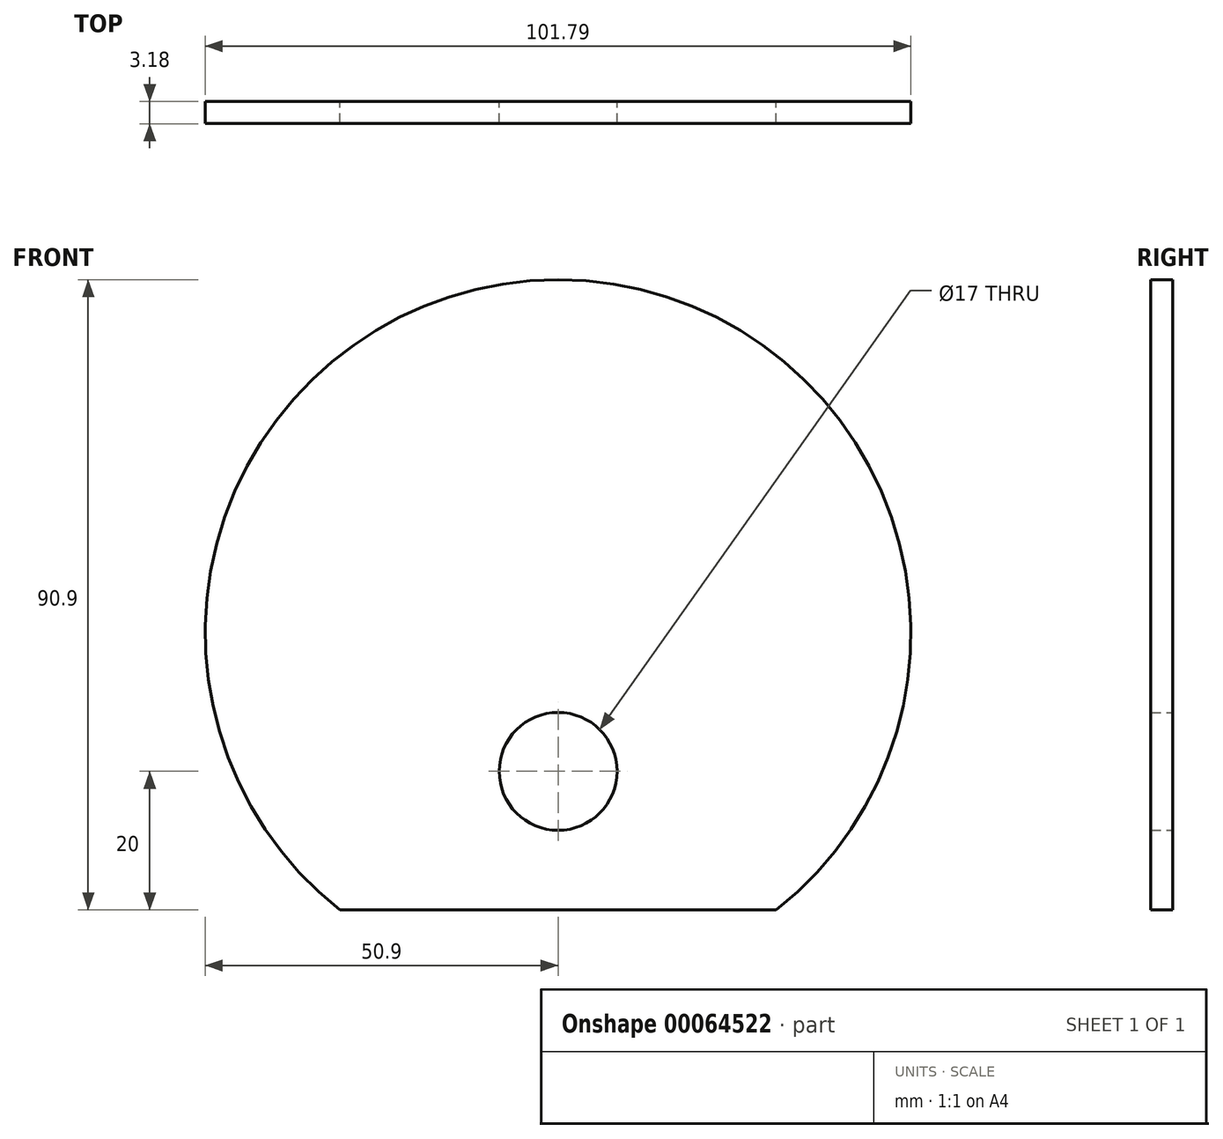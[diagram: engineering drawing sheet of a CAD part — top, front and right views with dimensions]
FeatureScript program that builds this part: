
annotation { "Feature Type Name" : "Feature", "Feature Type Description" : "" }
export const myFeature = defineFeature(function(context is Context, id is Id, definition is map)
    precondition{}
    {
        {
            var Q0;
            Q0=qCreatedBy(makeId("Front.planeOp"),FACE);
            var sketch = newSketch(context, id + "F0", { "sketchPlane" : qUnion([Q0])});
            skCircle(sketch, "E0", {"center": v(0, 0) * mm, "radius": 40 * mm});
            skCircle(sketch, "E1", {"center": v(0, 0) * mm, "radius": 50.9 * mm});
            skLineSegment(sketch, "E2.bottom", {"start": v(-55, -40) * mm, "end": v(55, -40) * mm});
            skLineSegment(sketch, "E2.top", {"start": v(-55, -70) * mm, "end": v(55, -70) * mm});
            skLineSegment(sketch, "E2.left", {"start": v(-55, -40) * mm, "end": v(-55, -70) * mm});
            skLineSegment(sketch, "E2.right", {"start": v(55, -40) * mm, "end": v(55, -70) * mm});
            skCircle(sketch, "E3", {"center": v(0, 0) * mm, "radius": 5 * mm});
            skCircle(sketch, "E4", {"center": v(0, -20) * mm, "radius": 8.5 * mm});
            skLineSegment(sketch, "E5.bottom", {"start": v(50, -45) * mm, "end": v(-50, -45) * mm});
            skLineSegment(sketch, "E5.top", {"start": v(50, -65) * mm, "end": v(-50, -65) * mm});
            skLineSegment(sketch, "E5.left", {"start": v(50, -45) * mm, "end": v(50, -65) * mm});
            skLineSegment(sketch, "E5.right", {"start": v(-50, -45) * mm, "end": v(-50, -65) * mm});
            skLineSegment(sketch, "E6", {"start": v(-50, -45) * mm, "end": v(-50, -40) * mm});
            skLineSegment(sketch, "E7", {"start": v(-50, -45) * mm, "end": v(-55, -45) * mm});
            skLineSegment(sketch, "E8", {"start": v(50, -65) * mm, "end": v(55, -65) * mm});
            skLineSegment(sketch, "E9", {"start": v(55, -65) * mm, "end": v(50, -65) * mm});
            skLineSegment(sketch, "E10", {"start": v(50, -70) * mm, "end": v(50, -65) * mm});
            skPoint(sketch, "E11", {"position": v(0, -65) * mm});
            skPoint(sketch, "E12", {"position": v(0, -45) * mm});
            skPoint(sketch, "E13", {"position": v(0, -40) * mm});
            skSolve(sketch);
        }
        {
            var Q0;
            Q0=makeQuery(id+"F0.imprint","IMPRINT",FACE,{"disambiguationData":[TD([[makeQuery(id+"F0.imprint","IMPRINT",EDGE,{"derivedFrom":sQuery(id+"F0.wireOp",EDGE,"E0")}),1.0]])]});
            var Q1;
            Q1=makeQuery(id+"F0.imprint","IMPRINT",FACE,{"disambiguationData":[TD([[makeQuery(id+"F0.imprint","IMPRINT",EDGE,{"derivedFrom":sQuery(id+"F0.wireOp",EDGE,"E0")}),-1.0]])]});
            var Q2;
            Q2=makeQuery(id+"F0.imprint","IMPRINT",FACE,{"disambiguationData":[TD([[makeQuery(id+"F0.imprint","IMPRINT",EDGE,{"derivedFrom":sQuery(id+"F0.wireOp",EDGE,"E3")}),1.0]])]});
            extrude(context, id + "F1", {"entities" : qUnion([Q0, Q1, Q2]), "depth" : 3.17 * mm});
        }
    });
